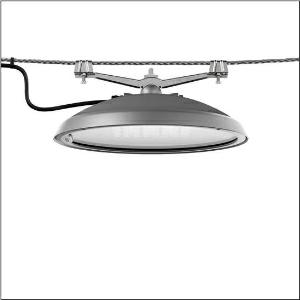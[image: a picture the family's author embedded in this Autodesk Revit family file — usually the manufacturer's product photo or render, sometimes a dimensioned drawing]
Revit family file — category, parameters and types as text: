
# Revit family: dl_r__50_iq_mini___st1_0s_5xa248w41f08he_3a14
name_source: partatom
category: Lighting Fixtures
units: mm (PartAtom-declared; Revit-internal decimal feet)

## family parameters
Cut with Voids When Loaded = No
Host = Face
Light Source = No
Part Type = Normal
Room Calculation Point = No
Round Connector Dimension = Use Diameter
Shared = No

## types (1)
- --- (1 x LED, 9400 lm, 64.6 W, 4000K)
    Apparent Load = 65 VA
    CIE Flux Codes = 37 72 97 100 100
    Color Rendering = 70
    Color Temperature = 4000K
    Default Elevation = 1800 mm
    Description = DL® 50 iQ mini, catenary luminaire, primary light control with lens, of PMMA, primary optical cover: cover, of toughened safety glass, transparent, light distribution: ST1.0s, light emission: direct distribution, primary light characteristic: symmetric, installation type: suspended mounting, LED, High Power LED, rated luminous flux: 9.400lm, luminous efficacy: 146lm/W, light colour: 740, colour temperature: 4000K, control: optimised constant luminous flux control (CLO 2.0), Desk-Remote (wireless, voltage-free reading and setting of iQ features in the workshop via application-optimized NFC function/RFID function), Light-Fading, Smart-Wire, Night-Set, Lumen-Switch, Temp-Guard, Auto-Match, Street-Remote, mains connection: 230..240V, AC, 50/60Hz, start of lifetime: 65W, end of service life: 68W, reduction: 29W, luminaire housing, of diecast aluminium, powder-coated, Siteco® metallic grey (DB 702S), diameter: 500mm, height: 115mm, protection rating (complete): IP66, insulation class (complete): insulation class II (safety insulation), certification: CE, ENEC, VDE, impact resistance: IK08, permissible operating ambient temperature for outdoor applications: -25..+40°C, standard-compliant lighting for roads and squares, packaging unit: 1 piece

Light Distribution: ST1.0s
    Height = 124 mm  [stored 0.406824 ft]
    Lamp = 1 x LED
    Lamp Light Flux = 9400 lm
    Lamp Power = 64.6 W
    Lamp count = 1
    Length = 500 mm
    Luminous efficacy = 146 lm/W
    Manufacturer = Siteco
    ModVariant = No
    Model = 5XA248W41F08HE
    Number of Poles = 1
    OnlyDefault = Yes
    Power Factor = 1
    Product Name = DL® 50 iQ mini | ST1.0s
    Product group = catenary luminaire
    ProductGroupID = 6300
    Protection Class = Protection class II
    Protection Degree = IP 66
    RLX_Detail_Level = 1
    RLX_Emergency_Light_Flux = 0 lm
    RLX_Emergency_Type = 0
    RLX_Emergency_Type_DB = No
    RlxData = <blob elided: 123205 chars, md5=ab12cd4e>
    Socket = socket
    Standby Power = 0 W
    System Light Flux = 9400 lm
    System Power = 65 W
    Type Comments = factory setting: luminous flux: 100 % | dim-lin: 254 | 655 mA
    Type Image = l_1242791.jpg
    URL = http://relux.com
    VarID = @adj_071927
    Voltage = 0 V
    Weight = 0.00 kg
    Width = 0 mm  [stored 0 ft]

note: [stored X ft] marks values corroborated as IEEE doubles in the binary element streams (Revit-internal decimal feet)

## geometry (parser evidence)
native form markers: Blend x4, Sweep x11
no freeform markers — native parametric forms only
